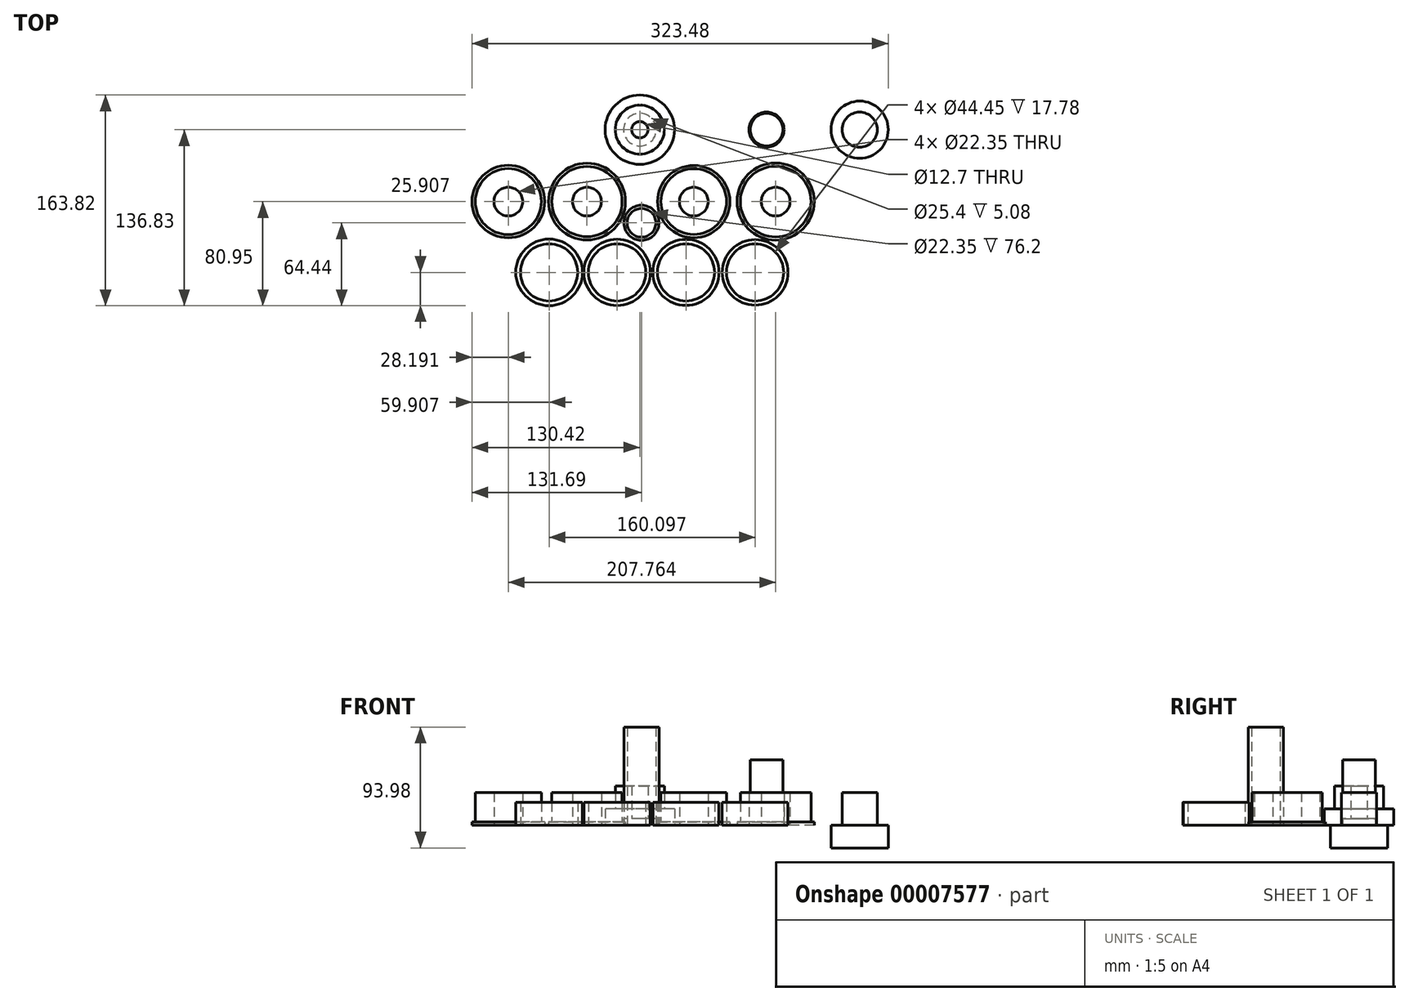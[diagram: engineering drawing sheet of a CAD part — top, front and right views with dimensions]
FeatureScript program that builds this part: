
annotation { "Feature Type Name" : "Feature", "Feature Type Description" : "" }
export const myFeature = defineFeature(function(context is Context, id is Id, definition is map)
    precondition{}
    {
        {
            var Q0;
            Q0=qCreatedBy(makeId("Top.planeOp"),FACE);
            var sketch = newSketch(context, id + "F0", { "sketchPlane" : qUnion([Q0])});
            skCircle(sketch, "E0", {"center": v(0, 0) * mm, "radius": 26.99 * mm});
            skCircle(sketch, "E1", {"center": v(0, 0) * mm, "radius": 19.05 * mm});
            skCircle(sketch, "E2", {"center": v(98.42, 0) * mm, "radius": 13.64 * mm});
            skCircle(sketch, "E3", {"center": v(170.84, 0) * mm, "radius": 13.64 * mm});
            skCircle(sketch, "E4", {"center": v(105.54, -55.88) * mm, "radius": 27.43 * mm});
            skCircle(sketch, "E5", {"center": v(105.54, -55.88) * mm, "radius": 11.18 * mm});
            skCircle(sketch, "E6", {"center": v(105.54, -55.88) * mm, "radius": 29.97 * mm});
            skCircle(sketch, "E7", {"center": v(-70.51, -110.92) * mm, "radius": 22.23 * mm});
            skCircle(sketch, "E8", {"center": v(-17.68, -110.92) * mm, "radius": 22.23 * mm});
            skCircle(sketch, "E9", {"center": v(35.81, -110.92) * mm, "radius": 22.23 * mm});
            skCircle(sketch, "E10", {"center": v(89.58, -110.92) * mm, "radius": 22.23 * mm});
            skCircle(sketch, "E11", {"center": v(-70.51, -110.92) * mm, "radius": 25.9 * mm});
            skCircle(sketch, "E12", {"center": v(-17.68, -110.92) * mm, "radius": 25.78 * mm});
            skCircle(sketch, "E13", {"center": v(35.81, -110.92) * mm, "radius": 25.65 * mm});
            skCircle(sketch, "E14", {"center": v(89.58, -110.92) * mm, "radius": 25.53 * mm});
            skCircle(sketch, "E15", {"center": v(-41.05, -55.88) * mm, "radius": 27.3 * mm});
            skCircle(sketch, "E16", {"center": v(-41.05, -55.88) * mm, "radius": 11.18 * mm});
            skCircle(sketch, "E17", {"center": v(-41.05, -55.88) * mm, "radius": 29.85 * mm});
            skCircle(sketch, "E18", {"center": v(-102.23, -55.88) * mm, "radius": 25.65 * mm});
            skCircle(sketch, "E19", {"center": v(-102.23, -55.88) * mm, "radius": 11.18 * mm});
            skCircle(sketch, "E20", {"center": v(-102.23, -55.88) * mm, "radius": 28.2 * mm});
            skCircle(sketch, "E21", {"center": v(41.9, -55.88) * mm, "radius": 25.53 * mm});
            skCircle(sketch, "E22", {"center": v(41.9, -55.88) * mm, "radius": 11.18 * mm});
            skCircle(sketch, "E23", {"center": v(41.9, -55.88) * mm, "radius": 28.07 * mm});
            skCircle(sketch, "E24", {"center": v(1.27, -72.39) * mm, "radius": 11.18 * mm});
            skCircle(sketch, "E25", {"center": v(1.27, -72.39) * mm, "radius": 13.64 * mm});
            skSolve(sketch);
        }
        {
            var Q0;
            Q0=makeQuery(id+"F0.imprint","IMPRINT",FACE,{"disambiguationData":[TD([[makeQuery(id+"F0.imprint","IMPRINT",EDGE,{"derivedFrom":sQuery(id+"F0.wireOp",EDGE,"E1")}),1.0]])]});
            extrude(context, id + "F1", {"entities" : qUnion([Q0]), "depth" : 30.48 * mm, "offsetDistance" : 25.4 * mm});
        }
        {
            var Q0;
            Q0=makeQuery(id+"F0.imprint","IMPRINT",FACE,{"disambiguationData":[TD([[makeQuery(id+"F0.imprint","IMPRINT",EDGE,{"derivedFrom":sQuery(id+"F0.wireOp",EDGE,"E0")}),1.0]])]});
            extrude(context, id + "F2", {"entities" : qUnion([Q0]), "operationType" : NewBodyOperationType.ADD, "depth" : 12.7 * mm, "offsetDistance" : 25.4 * mm});
        }
        {
            var Q0;
            Q0=sQuery(id+"F0.wireOp",VERTEX,"E0.center");
            var Q1;
            Q1=makeQuery(id+"F1.opExtrude","SWEPT_BODY",BODY,{"disambiguationData":[OSD([sQuery(id+"F0.wireOp",EDGE,"E1")])]});
            hole(context, id + "F3", {"style" : HoleStyle.SIMPLE, "endStyle" : HoleEndStyle.THROUGH, "oppositeDirection" : true, "holeDiameter" : 12.7 * mm, "majorDiameter" : 6.35 * mm, "isTappedThrough" : true, "tappedDepth" : 12.7 * mm, "tapClearance" : 3, "locations" : qUnion([Q0]), "scope" : qUnion([Q1])});
        }
        {
            var Q0;
            Q0=makeQuery(id+"F0.imprint","IMPRINT",FACE,{"disambiguationData":[TD([[makeQuery(id+"F0.imprint","IMPRINT",EDGE,{"derivedFrom":sQuery(id+"F0.wireOp",EDGE,"E0")}),1.0]])]});
            var sketch = newSketch(context, id + "F4", { "sketchPlane" : qUnion([Q0])});
            skCircle(sketch, "E26", {"center": v(0, 0) * mm, "radius": 12.7 * mm});
            skSolve(sketch);
        }
        {
            var Q0;
            Q0 = qSketchRegion(id + "F4", true);
            extrude(context, id + "F5", {"entities" : qUnion([Q0]), "operationType" : NewBodyOperationType.REMOVE, "depth" : 5.08 * mm, "offsetDistance" : 25.4 * mm});
        }
        {
            var Q0;
            Q0=makeQuery(id+"F0.imprint","IMPRINT",FACE,{"disambiguationData":[TD([[makeQuery(id+"F0.imprint","IMPRINT",EDGE,{"derivedFrom":sQuery(id+"F0.wireOp",EDGE,"E4")}),-1.0]])]});
            var Q1;
            Q1=makeQuery(id+"F0.imprint","IMPRINT",FACE,{"disambiguationData":[TD([[makeQuery(id+"F0.imprint","IMPRINT",EDGE,{"derivedFrom":sQuery(id+"F0.wireOp",EDGE,"E15")}),-1.0]])]});
            var Q2;
            Q2=makeQuery(id+"F0.imprint","IMPRINT",FACE,{"disambiguationData":[TD([[makeQuery(id+"F0.imprint","IMPRINT",EDGE,{"derivedFrom":sQuery(id+"F0.wireOp",EDGE,"E18")}),-1.0]])]});
            var Q3;
            Q3=makeQuery(id+"F0.imprint","IMPRINT",FACE,{"disambiguationData":[TD([[makeQuery(id+"F0.imprint","IMPRINT",EDGE,{"derivedFrom":sQuery(id+"F0.wireOp",EDGE,"E21")}),-1.0]])]});
            extrude(context, id + "F6", {"entities" : qUnion([Q0, Q1, Q2, Q3]), "depth" : 2.54 * mm, "offsetDistance" : 25.4 * mm});
        }
        {
            var Q0;
            Q0=makeQuery(id+"F0.imprint","IMPRINT",FACE,{"disambiguationData":[TD([[makeQuery(id+"F0.imprint","IMPRINT",EDGE,{"derivedFrom":sQuery(id+"F0.wireOp",EDGE,"E4")}),1.0]])]});
            var Q1;
            Q1=makeQuery(id+"F0.imprint","IMPRINT",FACE,{"disambiguationData":[TD([[makeQuery(id+"F0.imprint","IMPRINT",EDGE,{"derivedFrom":sQuery(id+"F0.wireOp",EDGE,"E2")}),1.0]])]});
            var Q2;
            Q2=makeQuery(id+"F0.imprint","IMPRINT",FACE,{"disambiguationData":[TD([[makeQuery(id+"F0.imprint","IMPRINT",EDGE,{"derivedFrom":sQuery(id+"F0.wireOp",EDGE,"E3")}),1.0]])]});
            var Q3;
            Q3=makeQuery(id+"F0.imprint","IMPRINT",FACE,{"disambiguationData":[TD([[makeQuery(id+"F0.imprint","IMPRINT",EDGE,{"derivedFrom":sQuery(id+"F0.wireOp",EDGE,"E15")}),1.0]])]});
            var Q4;
            Q4=makeQuery(id+"F0.imprint","IMPRINT",FACE,{"disambiguationData":[TD([[makeQuery(id+"F0.imprint","IMPRINT",EDGE,{"derivedFrom":sQuery(id+"F0.wireOp",EDGE,"E18")}),1.0]])]});
            var Q5;
            Q5=makeQuery(id+"F0.imprint","IMPRINT",FACE,{"disambiguationData":[TD([[makeQuery(id+"F0.imprint","IMPRINT",EDGE,{"derivedFrom":sQuery(id+"F0.wireOp",EDGE,"E21")}),1.0]])]});
            extrude(context, id + "F7", {"entities" : qUnion([Q0, Q1, Q2, Q3, Q4, Q5]), "operationType" : NewBodyOperationType.ADD, "depth" : 25.4 * mm, "offsetDistance" : 25.4 * mm});
        }
        {
            var Q0;
            Q0=makeQuery(id+"F7.opExtrude","CAP_FACE",FACE,{"disambiguationData":[OSD([sQuery(id+"F0.wireOp",EDGE,"E2")])],"isStart":false});
            var sketch = newSketch(context, id + "F8", { "sketchPlane" : qUnion([Q0])});
            skCircle(sketch, "E27", {"center": v(98.42, 0) * mm, "radius": 12.7 * mm});
            skSolve(sketch);
        }
        {
            var Q0;
            Q0=makeQuery(id+"F0.imprint","IMPRINT",FACE,{"disambiguationData":[TD([[makeQuery(id+"F0.imprint","IMPRINT",EDGE,{"derivedFrom":sQuery(id+"F0.wireOp",EDGE,"E3")}),1.0]])]});
            var sketch = newSketch(context, id + "F9", { "sketchPlane" : qUnion([Q0])});
            skCircle(sketch, "E28", {"center": v(170.84, 0) * mm, "radius": 22.23 * mm});
            skSolve(sketch);
        }
        {
            var Q0;
            Q0=makeQuery(id+"F9.imprint","IMPRINT",FACE,{"disambiguationData":[TD([[makeQuery(id+"F9.imprint","IMPRINT",EDGE,{"derivedFrom":sQuery(id+"F9.wireOp",EDGE,"E28")}),1.0]])]});
            var Q1;
            Q1=makeQuery(id+"F9.imprint","IMPRINT",FACE,{"disambiguationData":[TD([[makeQuery(id+"F9.imprint","IMPRINT",EDGE,{"derivedFrom":makeQuery(id+"F0.imprint","IMPRINT",EDGE,{"derivedFrom":sQuery(id+"F0.wireOp",EDGE,"E3")})}),1.0]])]});
            extrude(context, id + "F10", {"entities" : qUnion([Q0, Q1]), "operationType" : NewBodyOperationType.ADD, "oppositeDirection" : true, "depth" : 17.78 * mm, "offsetDistance" : 25.4 * mm});
        }
        {
            var Q0;
            Q0=makeQuery(id+"F8.imprint","IMPRINT",FACE,{"disambiguationData":[TD([[makeQuery(id+"F8.imprint","IMPRINT",EDGE,{"derivedFrom":sQuery(id+"F8.wireOp",EDGE,"E27")}),1.0]])]});
            extrude(context, id + "F11", {"entities" : qUnion([Q0]), "operationType" : NewBodyOperationType.ADD, "depth" : 25.4 * mm, "offsetDistance" : 25.4 * mm});
        }
        {
            var Q0;
            Q0=makeQuery(id+"F0.imprint","IMPRINT",FACE,{"disambiguationData":[TD([[makeQuery(id+"F0.imprint","IMPRINT",EDGE,{"derivedFrom":sQuery(id+"F0.wireOp",EDGE,"E7")}),-1.0]])]});
            var Q1;
            Q1=makeQuery(id+"F0.imprint","IMPRINT",FACE,{"disambiguationData":[TD([[makeQuery(id+"F0.imprint","IMPRINT",EDGE,{"derivedFrom":sQuery(id+"F0.wireOp",EDGE,"E8")}),-1.0]])]});
            var Q2;
            Q2=makeQuery(id+"F0.imprint","IMPRINT",FACE,{"disambiguationData":[TD([[makeQuery(id+"F0.imprint","IMPRINT",EDGE,{"derivedFrom":sQuery(id+"F0.wireOp",EDGE,"E9")}),-1.0]])]});
            var Q3;
            Q3=makeQuery(id+"F0.imprint","IMPRINT",FACE,{"disambiguationData":[TD([[makeQuery(id+"F0.imprint","IMPRINT",EDGE,{"derivedFrom":sQuery(id+"F0.wireOp",EDGE,"E10")}),-1.0]])]});
            extrude(context, id + "F12", {"entities" : qUnion([Q0, Q1, Q2, Q3]), "depth" : 17.78 * mm, "offsetDistance" : 25.4 * mm});
        }
        {
            var Q0;
            Q0=makeQuery(id+"F0.imprint","IMPRINT",FACE,{"disambiguationData":[TD([[makeQuery(id+"F0.imprint","IMPRINT",EDGE,{"derivedFrom":sQuery(id+"F0.wireOp",EDGE,"E24")}),-1.0]])]});
            extrude(context, id + "F13", {"entities" : qUnion([Q0]), "depth" : 76.2 * mm, "offsetDistance" : 25.4 * mm});
        }
    });
